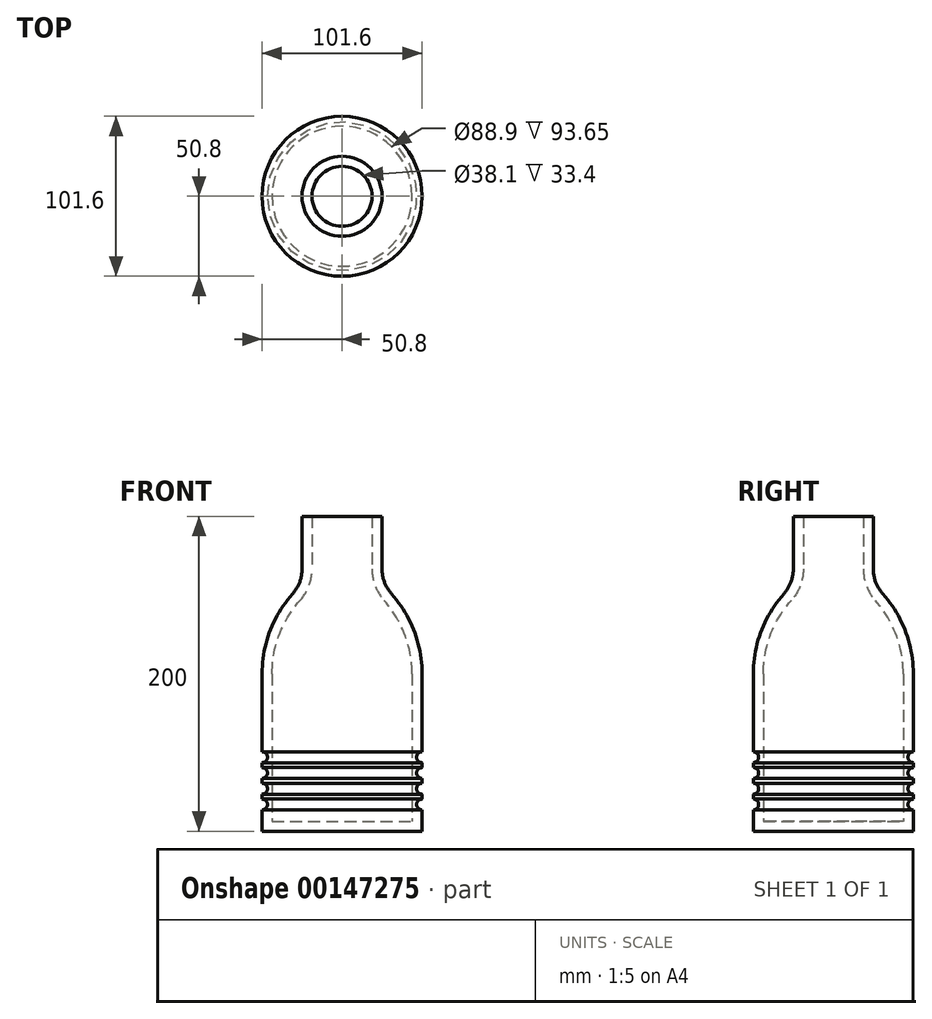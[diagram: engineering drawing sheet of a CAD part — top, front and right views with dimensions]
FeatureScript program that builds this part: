
annotation { "Feature Type Name" : "Feature", "Feature Type Description" : "" }
export const myFeature = defineFeature(function(context is Context, id is Id, definition is map)
    precondition{}
    {
        {
            var Q0;
            Q0=qCreatedBy(makeId("Front.planeOp"),FACE);
            var sketch = newSketch(context, id + "F0", { "sketchPlane" : qUnion([Q0])});
            skLineSegment(sketch, "E0", {"start": v(0, 6.35) * mm, "end": v(0, 55.78) * mm, "construction": true});
            skLineSegment(sketch, "E1", {"start": v(-44.45, 100) * mm, "end": v(-44.45, 6.35) * mm});
            skLineSegment(sketch, "E2", {"start": v(-19.05, 200) * mm, "end": v(-19.05, 166.6) * mm});
            skArc(sketch, "E3", {"start": v(-26.71, 146.51) * mm, "mid": v(-39.86, 124.9) * mm, "end": v(-44.45, 100) * mm});
            skLineSegment(sketch, "E4", {"start": v(-44.45, 6.35) * mm, "end": v(0, 6.35) * mm});
            skPoint(sketch, "E5.visualSharp", {"position": v(-19.05, 153.88) * mm});
            skArc(sketch, "E5.filletArc", {"start": v(-26.71, 146.51) * mm, "mid": v(-21.03, 155.85) * mm, "end": v(-19.05, 166.6) * mm});
            skLineSegment(sketch, "E6.0", {"start": v(-50.8, 0) * mm, "end": v(0, 0) * mm});
            skLineSegment(sketch, "E6.1", {"start": v(-25.4, 200) * mm, "end": v(-25.4, 166.6) * mm});
            skArc(sketch, "E6.2", {"start": v(-31.45, 150.74) * mm, "mid": v(-26.96, 158.11) * mm, "end": v(-25.4, 166.6) * mm});
            skArc(sketch, "E6.3", {"start": v(-31.45, 150.74) * mm, "mid": v(-45.8, 127.15) * mm, "end": v(-50.8, 100) * mm});
            skLineSegment(sketch, "E6.4", {"start": v(-50.8, 100) * mm, "end": v(-50.8, 50.4) * mm});
            skLineSegment(sketch, "E7", {"start": v(-25.4, 200) * mm, "end": v(-19.05, 200) * mm});
            skLineSegment(sketch, "E8", {"start": v(0, 6.35) * mm, "end": v(0, 0) * mm});
            skArc(sketch, "E9", {"start": v(-50.8, 13.54) * mm, "mid": v(-47.37, 16.97) * mm, "end": v(-50.8, 20.4) * mm});
            skLineSegment(sketch, "E10.trimOffspring", {"start": v(-50.8, 13.54) * mm, "end": v(-50.8, 0) * mm});
            skArc(sketch, "E11.0.1.0", {"start": v(-50.8, 23.54) * mm, "mid": v(-47.37, 26.97) * mm, "end": v(-50.8, 30.4) * mm});
            skArc(sketch, "E11.0.2.0", {"start": v(-50.8, 33.54) * mm, "mid": v(-47.37, 36.97) * mm, "end": v(-50.8, 40.4) * mm});
            skArc(sketch, "E11.0.3.0", {"start": v(-50.8, 43.54) * mm, "mid": v(-47.37, 46.97) * mm, "end": v(-50.8, 50.4) * mm});
            skLineSegment(sketch, "E11.direction1", {"start": v(-50.8, 13.54) * mm, "end": v(-25.8, 13.54) * mm, "construction": true});
            skLineSegment(sketch, "E11.direction2", {"start": v(-50.8, 13.54) * mm, "end": v(-50.8, 23.54) * mm, "construction": true});
            skLineSegment(sketch, "E12.trimOffspring", {"start": v(-50.8, 23.54) * mm, "end": v(-50.8, 20.4) * mm});
            skLineSegment(sketch, "E13.trimOffspring", {"start": v(-50.8, 33.54) * mm, "end": v(-50.8, 30.4) * mm});
            skLineSegment(sketch, "E14.trimOffspring", {"start": v(-50.8, 43.54) * mm, "end": v(-50.8, 40.4) * mm});
            skSolve(sketch);
        }
        {
            var Q0;
            Q0=makeQuery(id+"F0.imprint","IMPRINT",FACE,{"disambiguationData":[TD([[makeQuery(id+"F0.imprint","IMPRINT",EDGE,{"derivedFrom":sQuery(id+"F0.wireOp",EDGE,"E1")}),-1.0]])]});
            var Q1;
            Q1=sQuery(id+"F0.wireOp",EDGE,"E0");
            revolve(context, id + "F1", {"entities" : qUnion([Q0]), "axis" : qUnion([Q1]), "revolveType" : RevolveType.FULL});
        }
    });
